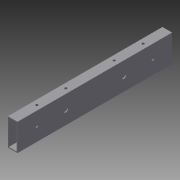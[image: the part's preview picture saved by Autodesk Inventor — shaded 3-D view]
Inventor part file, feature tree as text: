
AUTODESK INVENTOR PART (.ipt)
format: ipt  version: 2015 (Build 190159000, 159)  size: 126,976 bytes
history: native  units: in
note: dims shown in document units (in); Inventor stores cm internally (conversion verified against a paired STEP export)
features: sketch x5, hole x4, extrude x1, projected_geometry x1
ambient origin geometry x8: Origin, YZ Plane, XZ Plane, XY Plane, X Axis, Y Axis, Z Axis, Center Point
bodies: Solid1 (feature_tree)
feature tree (11):
  extrude  "Extrusion1"  Depth=0.5in
  hole  "Hole1"  [1 undecoded]
  hole  "Hole2"  [1 undecoded]
  hole  "Hole3"  [1 undecoded]
  hole  "Hole4"  [1 undecoded]
  sketch  "Sketch1"  dims[d0=1.4in d1=0.5in]
  sketch  "Sketch2"  dims[d2=0.05in d3=8.0in d4=0.0in]
  sketch  "Sketch3"  dims[d5=0.7in d6=1.0in]
  sketch  "Sketch4"  dims[d7=1.0in]
  projected_geometry  "Projected Loop1"
  sketch  "Sketch5"  dims[d11=0.1285in d12=0.75in d13=0.375in d14=0.25in d15=0.5635in d16=1.0in d17=0.8108in d18=1.5in d19=1.5in d20=0.257in d21=0.75in d22=0.375in d23=0.25in d24=0.5635in d25=1.0in d26=0.8108in d27=0.25in d28=1.25in d29=1.25in d30=0.128in d31=0.75in d32=0.375in d33=0.25in d34=0.5635in d35=1.0in d36=0.8108in d37=4.0in d38=0.25in d39=1.25in d40=1.25in d41=0.125in d42=0.75in d43=0.375in d44=0.25in d45=0.5635in d46=1.0in d47=0.8108in]
note: 4 required parameter values undecoded (feature->parameter linkage not recoverable at this tier; creation-order binding heuristic only, values carry confidence <= 0.55)
